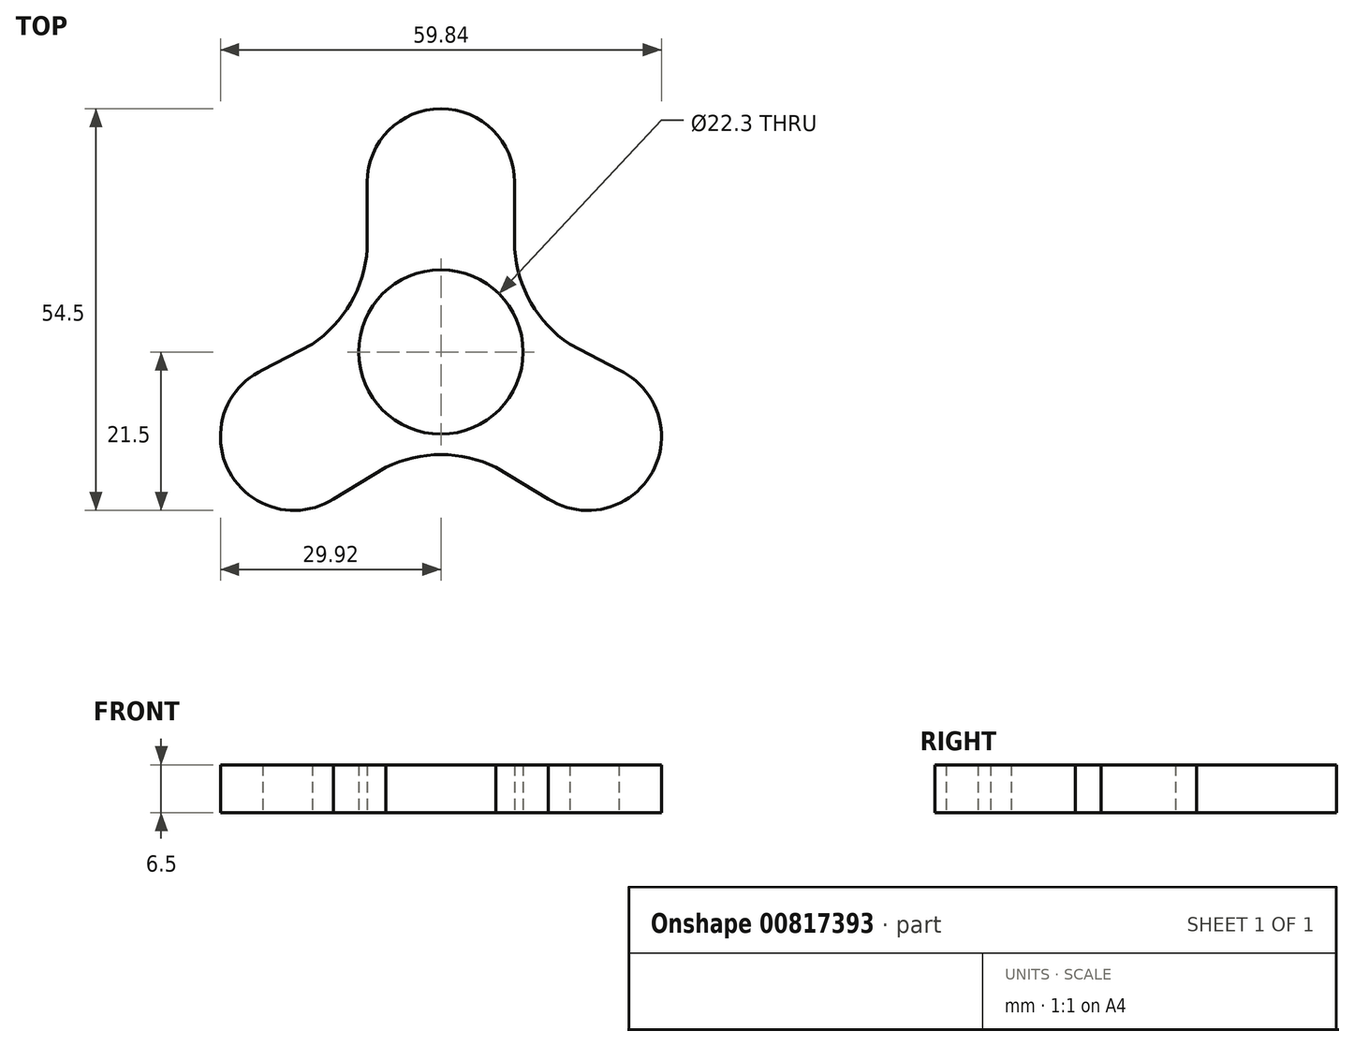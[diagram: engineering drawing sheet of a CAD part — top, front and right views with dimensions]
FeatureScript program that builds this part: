
annotation { "Feature Type Name" : "Feature", "Feature Type Description" : "" }
export const myFeature = defineFeature(function(context is Context, id is Id, definition is map)
    precondition{}
    {
        {
            var Q0;
            Q0=qCreatedBy(makeId("Top.planeOp"),FACE);
            var sketch = newSketch(context, id + "F0", { "sketchPlane" : qUnion([Q0])});
            skCircle(sketch, "E0", {"center": v(0, 0) * mm, "radius": 11.15 * mm});
            skLineSegment(sketch, "E1", {"start": v(0, 0) * mm, "end": v(0, 23) * mm});
            skCircle(sketch, "E2", {"center": v(0, 23) * mm, "radius": 10 * mm});
            skCircle(sketch, "E3.cCircle", {"center": v(0, 0) * mm, "radius": 23 * mm, "construction": true});
            skLineSegment(sketch, "E3.0", {"start": v(0, 23) * mm, "end": v(19.92, -11.5) * mm});
            skLineSegment(sketch, "E3.1", {"start": v(19.92, -11.5) * mm, "end": v(-19.92, -11.5) * mm});
            skLineSegment(sketch, "E3.2", {"start": v(-19.92, -11.5) * mm, "end": v(0, 23) * mm});
            skCircle(sketch, "E4", {"center": v(-19.92, -11.5) * mm, "radius": 10 * mm});
            skCircle(sketch, "E5", {"center": v(19.92, -11.5) * mm, "radius": 10 * mm});
            skLineSegment(sketch, "E6", {"start": v(0, 23) * mm, "end": v(-10, 23) * mm});
            skLineSegment(sketch, "E7", {"start": v(-10, 23) * mm, "end": v(-10, 4.93) * mm});
            skLineSegment(sketch, "E8", {"start": v(0, 23) * mm, "end": v(10, 23) * mm});
            skLineSegment(sketch, "E9", {"start": v(10, 23) * mm, "end": v(10, 4.93) * mm});
            skLineSegment(sketch, "E10", {"start": v(19.92, -11.5) * mm, "end": v(24.92, -2.84) * mm});
            skLineSegment(sketch, "E11", {"start": v(19.92, -11.5) * mm, "end": v(14.92, -20.16) * mm});
            skLineSegment(sketch, "E12", {"start": v(-19.92, -11.5) * mm, "end": v(-14.92, -20.16) * mm});
            skLineSegment(sketch, "E13", {"start": v(-19.92, -11.5) * mm, "end": v(-24.92, -2.84) * mm});
            skLineSegment(sketch, "E14", {"start": v(-24.92, -2.84) * mm, "end": v(-10, 4.93) * mm});
            skLineSegment(sketch, "E15", {"start": v(10, 4.93) * mm, "end": v(24.92, -2.84) * mm});
            skLineSegment(sketch, "E16", {"start": v(0, 0) * mm, "end": v(0, -11.15) * mm});
            skLineSegment(sketch, "E17", {"start": v(0, -11.15) * mm, "end": v(-14.92, -20.16) * mm});
            skLineSegment(sketch, "E18", {"start": v(0, -11.15) * mm, "end": v(14.92, -20.16) * mm});
            skArc(sketch, "E19", {"start": v(-17.46, 1.05) * mm, "mid": v(-12.24, 6.64) * mm, "end": v(-10, 13.97) * mm});
            skArc(sketch, "E20", {"start": v(10, 13.97) * mm, "mid": v(12.24, 6.64) * mm, "end": v(17.46, 1.05) * mm});
            skArc(sketch, "E21", {"start": v(7.46, -15.66) * mm, "mid": v(0, -13.93) * mm, "end": v(-7.46, -15.66) * mm});
            skSolve(sketch);
        }
        {
            var Q0;
            Q0=qSketchRegion(id+"F0",true);
            var Q1;
            {var subQ5=sQuery(id+"F0.wireOp",EDGE,"E17");var subQ6=sQuery(id+"F0.wireOp",EDGE,"E3.1");var subQ7=makeQuery(id+"F0.imprint","INTERSECT",VERTEX,{"derivedFrom":[subQ6,subQ5]});Q1=makeQuery(id+"F0.imprint","IMPRINT",FACE,{"disambiguationData":[TD([[makeQuery(id+"F0.imprint","IMPRINT",EDGE,{"disambiguationData":[TD([[subQ7,-1.0]])],"derivedFrom":subQ6}),-1.0]])]});}
            var Q2;
            {var subQ1=sQuery(id+"F0.wireOp",EDGE,"E3.1");var subQ3=sQuery(id+"F0.wireOp",EDGE,"E4");var subQ4=makeQuery(id+"F0.imprint","INTERSECT",VERTEX,{"derivedFrom":[subQ1,subQ3]});Q2=makeQuery(id+"F0.imprint","IMPRINT",FACE,{"disambiguationData":[TD([[makeQuery(id+"F0.imprint","IMPRINT",EDGE,{"disambiguationData":[TD([[subQ4,-1.0]])],"derivedFrom":subQ3}),1.0]])]});}
            var Q3;
            {var subQ0=sQuery(id+"F0.wireOp",EDGE,"E14");var subQ1=sQuery(id+"F0.wireOp",EDGE,"E3.2");var subQ2=makeQuery(id+"F0.imprint","INTERSECT",VERTEX,{"derivedFrom":[subQ1,subQ0]});Q3=makeQuery(id+"F0.imprint","IMPRINT",FACE,{"disambiguationData":[TD([[makeQuery(id+"F0.imprint","IMPRINT",EDGE,{"disambiguationData":[TD([[subQ2,-1.0]])],"derivedFrom":subQ1}),-1.0]])]});}
            var Q4;
            {var subQ1=sQuery(id+"F0.wireOp",EDGE,"E1");var subQ6=sQuery(id+"F0.wireOp",EDGE,"E0");var subQ9=makeQuery(id+"F0.imprint","INTERSECT",VERTEX,{"derivedFrom":[subQ6,subQ1]});Q4=makeQuery(id+"F0.imprint","IMPRINT",FACE,{"disambiguationData":[TD([[makeQuery(id+"F0.imprint","IMPRINT",EDGE,{"disambiguationData":[TD([[subQ9,-1.0]])],"derivedFrom":subQ1}),1.0]])]});}
            var Q5;
            {var subQ1=sQuery(id+"F0.wireOp",EDGE,"E1");var subQ3=sQuery(id+"F0.wireOp",EDGE,"E2");var subQ4=makeQuery(id+"F0.imprint","INTERSECT",VERTEX,{"derivedFrom":[subQ1,subQ3]});Q5=makeQuery(id+"F0.imprint","IMPRINT",FACE,{"disambiguationData":[TD([[makeQuery(id+"F0.imprint","IMPRINT",EDGE,{"disambiguationData":[TD([[subQ4,1.0]])],"derivedFrom":subQ3}),1.0]])]});}
            var Q6;
            {var subQ1=sQuery(id+"F0.wireOp",EDGE,"E1");var subQ3=sQuery(id+"F0.wireOp",EDGE,"E2");var subQ4=makeQuery(id+"F0.imprint","INTERSECT",VERTEX,{"derivedFrom":[subQ1,subQ3]});Q6=makeQuery(id+"F0.imprint","IMPRINT",FACE,{"disambiguationData":[TD([[makeQuery(id+"F0.imprint","IMPRINT",EDGE,{"disambiguationData":[TD([[subQ4,-1.0]])],"derivedFrom":subQ3}),1.0]])]});}
            var Q7;
            {var subQ5=sQuery(id+"F0.wireOp",EDGE,"E0");var subQ7=sQuery(id+"F0.wireOp",EDGE,"E1");var subQ9=makeQuery(id+"F0.imprint","INTERSECT",VERTEX,{"derivedFrom":[subQ5,subQ7]});Q7=makeQuery(id+"F0.imprint","IMPRINT",FACE,{"disambiguationData":[TD([[makeQuery(id+"F0.imprint","IMPRINT",EDGE,{"disambiguationData":[TD([[subQ9,-1.0]])],"derivedFrom":subQ7}),-1.0]])]});}
            var Q8;
            {var subQ0=sQuery(id+"F0.wireOp",EDGE,"E9");var subQ1=sQuery(id+"F0.wireOp",EDGE,"E3.0");var subQ2=makeQuery(id+"F0.imprint","INTERSECT",VERTEX,{"derivedFrom":[subQ1,subQ0]});Q8=makeQuery(id+"F0.imprint","IMPRINT",FACE,{"disambiguationData":[TD([[makeQuery(id+"F0.imprint","IMPRINT",EDGE,{"disambiguationData":[TD([[subQ2,-1.0]])],"derivedFrom":subQ1}),-1.0]])]});}
            var Q9;
            {var subQ1=sQuery(id+"F0.wireOp",EDGE,"E3.0");var subQ5=sQuery(id+"F0.wireOp",EDGE,"E15");var subQ6=makeQuery(id+"F0.imprint","INTERSECT",VERTEX,{"derivedFrom":[subQ1,subQ5]});Q9=makeQuery(id+"F0.imprint","IMPRINT",FACE,{"disambiguationData":[TD([[makeQuery(id+"F0.imprint","IMPRINT",EDGE,{"disambiguationData":[TD([[subQ6,-1.0]])],"derivedFrom":subQ1}),-1.0]])]});}
            var Q10;
            {var subQ1=sQuery(id+"F0.wireOp",EDGE,"E3.0");var subQ3=sQuery(id+"F0.wireOp",EDGE,"E5");var subQ4=makeQuery(id+"F0.imprint","INTERSECT",VERTEX,{"derivedFrom":[subQ1,subQ3]});Q10=makeQuery(id+"F0.imprint","IMPRINT",FACE,{"disambiguationData":[TD([[makeQuery(id+"F0.imprint","IMPRINT",EDGE,{"disambiguationData":[TD([[subQ4,-1.0]])],"derivedFrom":subQ3}),1.0]])]});}
            var Q11;
            {var subQ0=sQuery(id+"F0.wireOp",EDGE,"E18");var subQ1=sQuery(id+"F0.wireOp",EDGE,"E3.1");var subQ2=makeQuery(id+"F0.imprint","INTERSECT",VERTEX,{"derivedFrom":[subQ1,subQ0]});Q11=makeQuery(id+"F0.imprint","IMPRINT",FACE,{"disambiguationData":[TD([[makeQuery(id+"F0.imprint","IMPRINT",EDGE,{"disambiguationData":[TD([[subQ2,-1.0]])],"derivedFrom":subQ1}),-1.0]])]});}
            var Q12;
            {var subQ0=sQuery(id+"F0.wireOp",EDGE,"E3.2");var subQ1=sQuery(id+"F0.wireOp",EDGE,"E0");var subQ2=makeQuery(id+"F0.imprint","INTERSECT",VERTEX,{"disambiguationData":[OD(1.0)],"derivedFrom":[subQ1,subQ0]});Q12=makeQuery(id+"F0.imprint","IMPRINT",FACE,{"disambiguationData":[TD([[makeQuery(id+"F0.imprint","IMPRINT",EDGE,{"disambiguationData":[TD([[subQ2,-1.0]])],"derivedFrom":subQ1}),-1.0]])]});}
            var Q13;
            {var subQ0=sQuery(id+"F0.wireOp",EDGE,"E3.0");var subQ1=sQuery(id+"F0.wireOp",EDGE,"E0");var subQ2=makeQuery(id+"F0.imprint","INTERSECT",VERTEX,{"disambiguationData":[OD(0.0)],"derivedFrom":[subQ1,subQ0]});Q13=makeQuery(id+"F0.imprint","IMPRINT",FACE,{"disambiguationData":[TD([[makeQuery(id+"F0.imprint","IMPRINT",EDGE,{"disambiguationData":[TD([[subQ2,1.0]])],"derivedFrom":subQ1}),-1.0]])]});}
            extrude(context, id + "F1", {"entities" : qUnion([Q0, Q1, Q2, Q3, Q4, Q5, Q6, Q7, Q8, Q9, Q10, Q11, Q12, Q13]), "depth" : 6.5 * mm, "offsetDistance" : 25 * mm});
        }
    });
